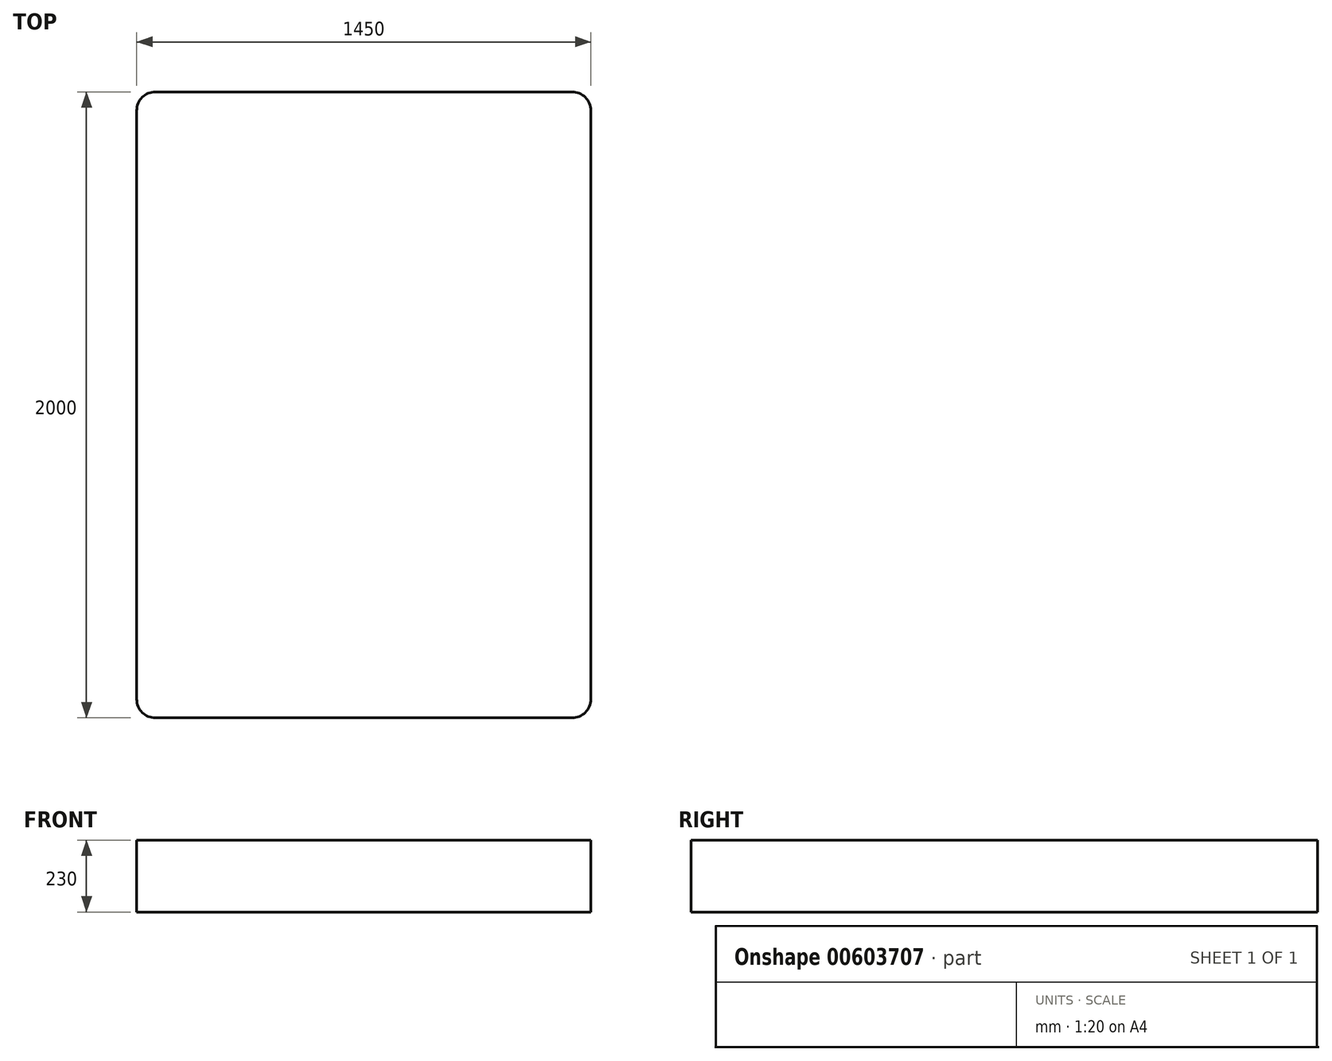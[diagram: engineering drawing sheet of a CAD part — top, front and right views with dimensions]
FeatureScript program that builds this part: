
annotation { "Feature Type Name" : "Feature", "Feature Type Description" : "" }
export const myFeature = defineFeature(function(context is Context, id is Id, definition is map)
    precondition{}
    {
        {
            var Q0;
            Q0=qCreatedBy(makeId("Top.planeOp"),FACE);
            var sketch = newSketch(context, id + "F0", { "sketchPlane" : qUnion([Q0])});
            skLineSegment(sketch, "E0.bottom", {"start": v(-665, 1000) * mm, "end": v(665, 1000) * mm});
            skLineSegment(sketch, "E0.top", {"start": v(-665, -1000) * mm, "end": v(665, -1000) * mm});
            skLineSegment(sketch, "E0.left", {"start": v(-725, 940) * mm, "end": v(-725, -940) * mm});
            skLineSegment(sketch, "E0.right", {"start": v(725, 940) * mm, "end": v(725, -940) * mm});
            skPoint(sketch, "E0.middle", {"position": v(0, 0) * mm});
            skPoint(sketch, "E1.visualSharp", {"position": v(-725, 1000) * mm});
            skArc(sketch, "E1.filletArc", {"start": v(-665, 1000) * mm, "mid": v(-707.43, 982.43) * mm, "end": v(-725, 940) * mm});
            skPoint(sketch, "E2.visualSharp", {"position": v(725, 1000) * mm});
            skArc(sketch, "E2.filletArc", {"start": v(725, 940) * mm, "mid": v(707.43, 982.43) * mm, "end": v(665, 1000) * mm});
            skPoint(sketch, "E3.visualSharp", {"position": v(-725, -1000) * mm});
            skArc(sketch, "E3.filletArc", {"start": v(-725, -940) * mm, "mid": v(-707.43, -982.43) * mm, "end": v(-665, -1000) * mm});
            skPoint(sketch, "E4.visualSharp", {"position": v(725, -1000) * mm});
            skArc(sketch, "E4.filletArc", {"start": v(665, -1000) * mm, "mid": v(707.43, -982.43) * mm, "end": v(725, -940) * mm});
            skSolve(sketch);
        }
        {
            var Q0;
            Q0 = qSketchRegion(id + "F0", true);
            extrude(context, id + "F1", {"entities" : qUnion([Q0]), "endBound" : BoundingType.SYMMETRIC, "depth" : 230 * mm, "offsetDistance" : 25.4 * mm});
        }
    });
